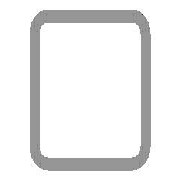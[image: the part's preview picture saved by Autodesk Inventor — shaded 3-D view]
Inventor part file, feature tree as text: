
AUTODESK INVENTOR PART (.ipt)
format: ipt  version: 2022 (Build 260153000, 153)  size: 134,656 bytes
history: native  units: mm (DEFAULTED — no unit token found)
features: other x4, sketch x3, extrude x1, plane x1
ambient origin geometry x8: Origin, YZ Plane, XZ Plane, XY Plane, X Axis, Y Axis, Z Axis, Center Point
bodies: Solid1 (feature_tree)
feature tree (9):
  parser-record x1  (decoder bookkeeping rows leaked as tree rows — omitted from the tree; the rows remain in map.json)
  other  "Driven Length"
  other  "Plano inicial"
  other  "Plano final"
  extrude  "Cuerpo"  TaperAngle=0.0deg  [1 undecoded]
  sketch  "Boceto"  dims[d10=40.0mm d11=40.0mm d12=5.0mm d13=-0.0mm d14=480.0mm d15=20.0mm d16=20.0mm d17=90.0deg d18=480.0mm]
  sketch  "Sketch3"  dims[d3=480.0mm d4=0.0mm]
  plane  "Work Plane3"
  sketch  "Sketch4"  dims[d7=7.5mm]
note: 1 required parameter value undecoded (feature->parameter linkage not recoverable at this tier; creation-order binding heuristic only, values carry confidence <= 0.55)
